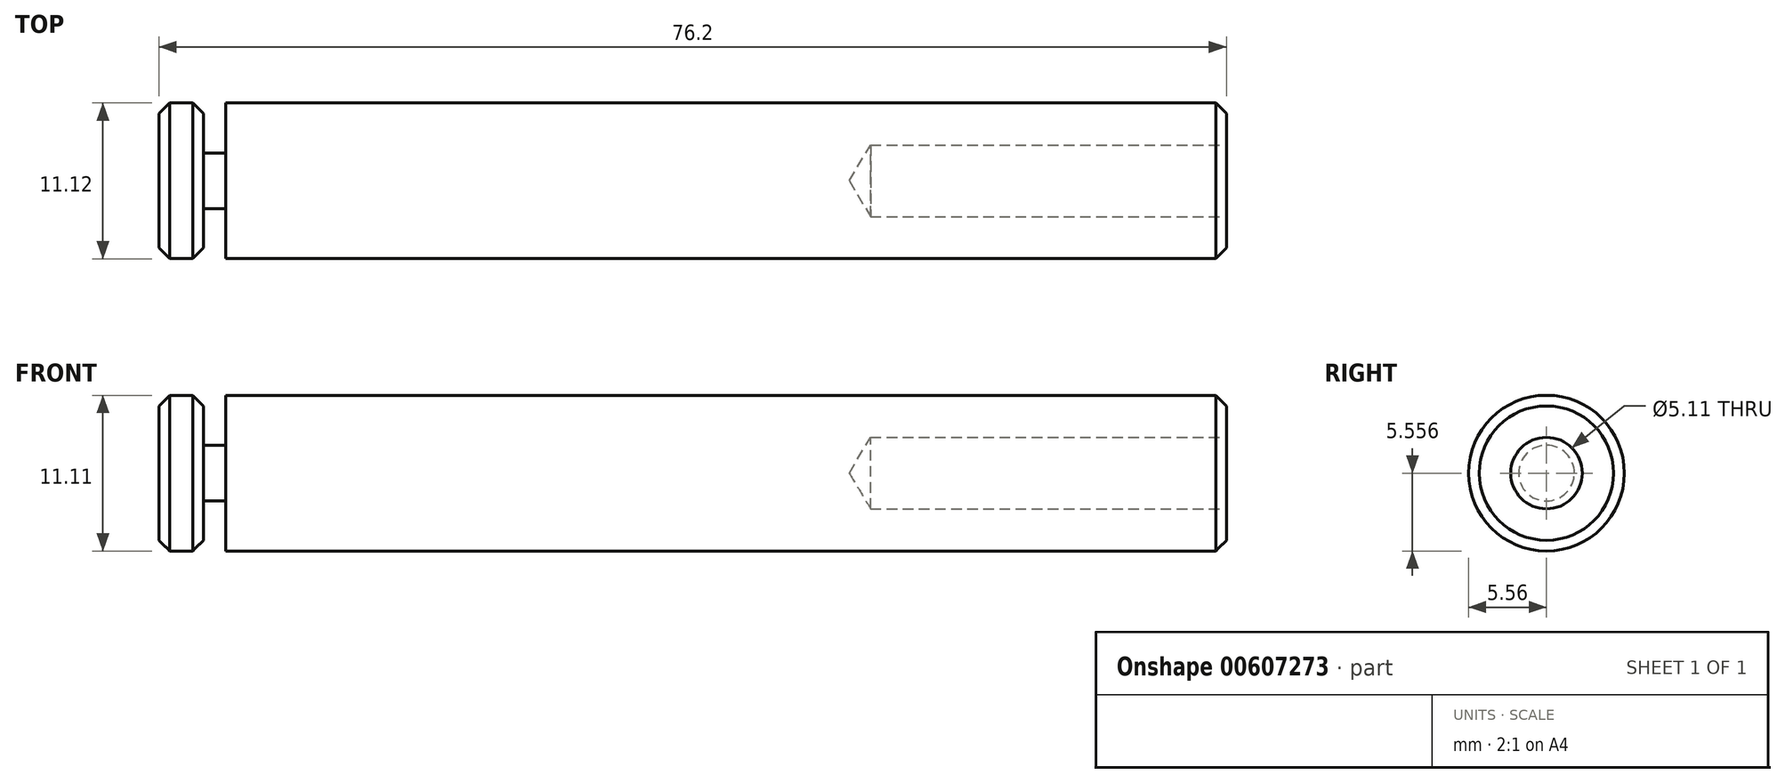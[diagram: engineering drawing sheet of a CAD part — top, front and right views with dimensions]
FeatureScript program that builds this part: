
annotation { "Feature Type Name" : "Feature", "Feature Type Description" : "" }
export const myFeature = defineFeature(function(context is Context, id is Id, definition is map)
    precondition{}
    {
        {
            var Q0;
            Q0=qCreatedBy(makeId("Front.planeOp"),FACE);
            var sketch = newSketch(context, id + "F0", { "sketchPlane" : qUnion([Q0])});
            skLineSegment(sketch, "E0", {"start": v(76.2, 0) * mm, "end": v(76.2, 5.56) * mm});
            skLineSegment(sketch, "E1", {"start": v(0, 0) * mm, "end": v(0, 5.56) * mm});
            skLineSegment(sketch, "E2", {"start": v(0, 5.56) * mm, "end": v(0, 0) * mm});
            skLineSegment(sketch, "E3", {"start": v(0, 5.56) * mm, "end": v(76.2, 5.56) * mm});
            skLineSegment(sketch, "E4", {"start": v(0, 0) * mm, "end": v(3.18, 0) * mm, "construction": true});
            skLineSegment(sketch, "E5", {"start": v(4.76, 0) * mm, "end": v(4.76, 3.57) * mm});
            skLineSegment(sketch, "E6", {"start": v(4.76, 3.57) * mm, "end": v(4.76, 0) * mm});
            skLineSegment(sketch, "E7", {"start": v(3.18, 0) * mm, "end": v(3.18, 3.57) * mm});
            skLineSegment(sketch, "E8", {"start": v(3.18, 3.57) * mm, "end": v(4.76, 3.57) * mm});
            skLineSegment(sketch, "E9", {"start": v(3.18, 0) * mm, "end": v(0, 0) * mm});
            skLineSegment(sketch, "E10", {"start": v(4.76, 0) * mm, "end": v(76.2, 0) * mm});
            skSolve(sketch);
        }
        {
            var Q0;
            Q0 = qSketchRegion(id + "F0", true);
            var Q1;
            Q1=sQuery(id+"F0.wireOp",EDGE,"E3");
            revolve(context, id + "F1", {"entities" : qUnion([Q0]), "axis" : qUnion([Q1]), "revolveType" : RevolveType.FULL});
        }
        {
            var Q0;
            Q0=makeQuery(id+"F1.opRevolve","SWEPT_EDGE",EDGE,{"disambiguationData":[OSD([sQuery(id+"F0.wireOp",EDGE,"E2"),sQuery(id+"F0.wireOp",EDGE,"E9")])]});
            var Q1;
            Q1=makeQuery(id+"F1.opRevolve","SWEPT_EDGE",EDGE,{"disambiguationData":[OSD([sQuery(id+"F0.wireOp",EDGE,"E0"),sQuery(id+"F0.wireOp",EDGE,"E10")])]});
            chamfer(context, id + "F2", {"entities" : qUnion([Q0, Q1]), "width" : 0.76 * mm, "tangentPropagation" : true});
        }
        {
            var Q0;
            Q0=makeQuery(id+"F1.opRevolve","SWEPT_FACE",FACE,{"disambiguationData":[OSD([sQuery(id+"F0.wireOp",EDGE,"E0")])]});
            var sketch = newSketch(context, id + "F3", { "sketchPlane" : qUnion([Q0])});
            skPoint(sketch, "E11", {"position": v(0, 5.56) * mm});
            skSolve(sketch);
        }
        {
            var Q0;
            Q0=sQuery(id+"F3.wireOp",VERTEX,"E11");
            var Q1;
            Q1=makeQuery(id+"F1.opRevolve","SWEPT_BODY",BODY,{"disambiguationData":[OSD([sQuery(id+"F0.wireOp",EDGE,"E0"),sQuery(id+"F0.wireOp",EDGE,"E2"),sQuery(id+"F0.wireOp",EDGE,"E3"),sQuery(id+"F0.wireOp",EDGE,"E6"),sQuery(id+"F0.wireOp",EDGE,"E7"),sQuery(id+"F0.wireOp",EDGE,"E8"),sQuery(id+"F0.wireOp",EDGE,"E9"),sQuery(id+"F0.wireOp",EDGE,"E10")])]});
            hole(context, id + "F4", {"style" : HoleStyle.SIMPLE, "endStyle" : HoleEndStyle.BLIND, "standardTappedOrClearance" : lookupTablePath({ "standard" : "ANSI", "engagement" : "75%", "pitch" : "20 tpi", "size" : "1/4", "type" : "Tapped" }), "standardBlindInLast" : lookupTablePath({ "standard" : "ANSI", "engagement" : "75%", "pitch" : "20 tpi", "size" : "1/4", "type" : "Tapped" }), "holeDiameter" : 5.1 * mm, "majorDiameter" : 6.35 * mm, "showTappedDepth" : true, "holeDepth" : 25.4 * mm, "isTappedThrough" : true, "tappedDepth" : 21.59 * mm, "tapClearance" : 20, "locations" : qUnion([Q0]), "scope" : qUnion([Q1])});
        }
    });
